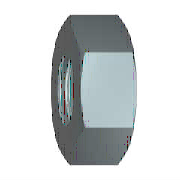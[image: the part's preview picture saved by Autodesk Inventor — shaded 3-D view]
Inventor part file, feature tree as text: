
AUTODESK INVENTOR PART (.ipt)
format: ipt  version: 2016 (Build 200138000, 138)  size: 163,328 bytes
history: native  units: mm (DEFAULTED — no unit token found)
features: sketch x3, chamfer x1, hole x1, other x1, plane x1
ambient origin geometry x7: Origin, YZ Plane, XZ Plane, X Axis, Y Axis, Z Axis, Center Point
bodies: Solid1 (feature_tree), Body (feature_tree)
feature tree (7):
  chamfer  "Chamfer1"  Angle=30.0deg  [1 undecoded]
  hole  "Thread"  [1 undecoded]
  other  "Work Axis1"
  plane  "Work Plane1"
  sketch  "Sketch1"  dims[d0=8.082904mm]
  sketch  "Sketch2"  dims[d1=3.2mm]
  sketch  "Sketch3"  dims[d2=0.0mm d3=30.0deg d4=30.0deg d5=5.9mm d6=5.9mm d7=90.0deg d25=3.242mm d26=6.0mm d27=4.0mm d28=2.0mm d29=14.3117mm d30=8.0mm d31=20.594885mm d8=0.378886mm d9=30.0deg d10=0.378886mm d11=30.0deg d13=0.0mm d14=0.0mm d39=0.0mm d40=0.378886mm d41=0.378886mm d42=0.0mm]
note: 2 required parameter values undecoded (feature->parameter linkage not recoverable at this tier; creation-order binding heuristic only, values carry confidence <= 0.55)
